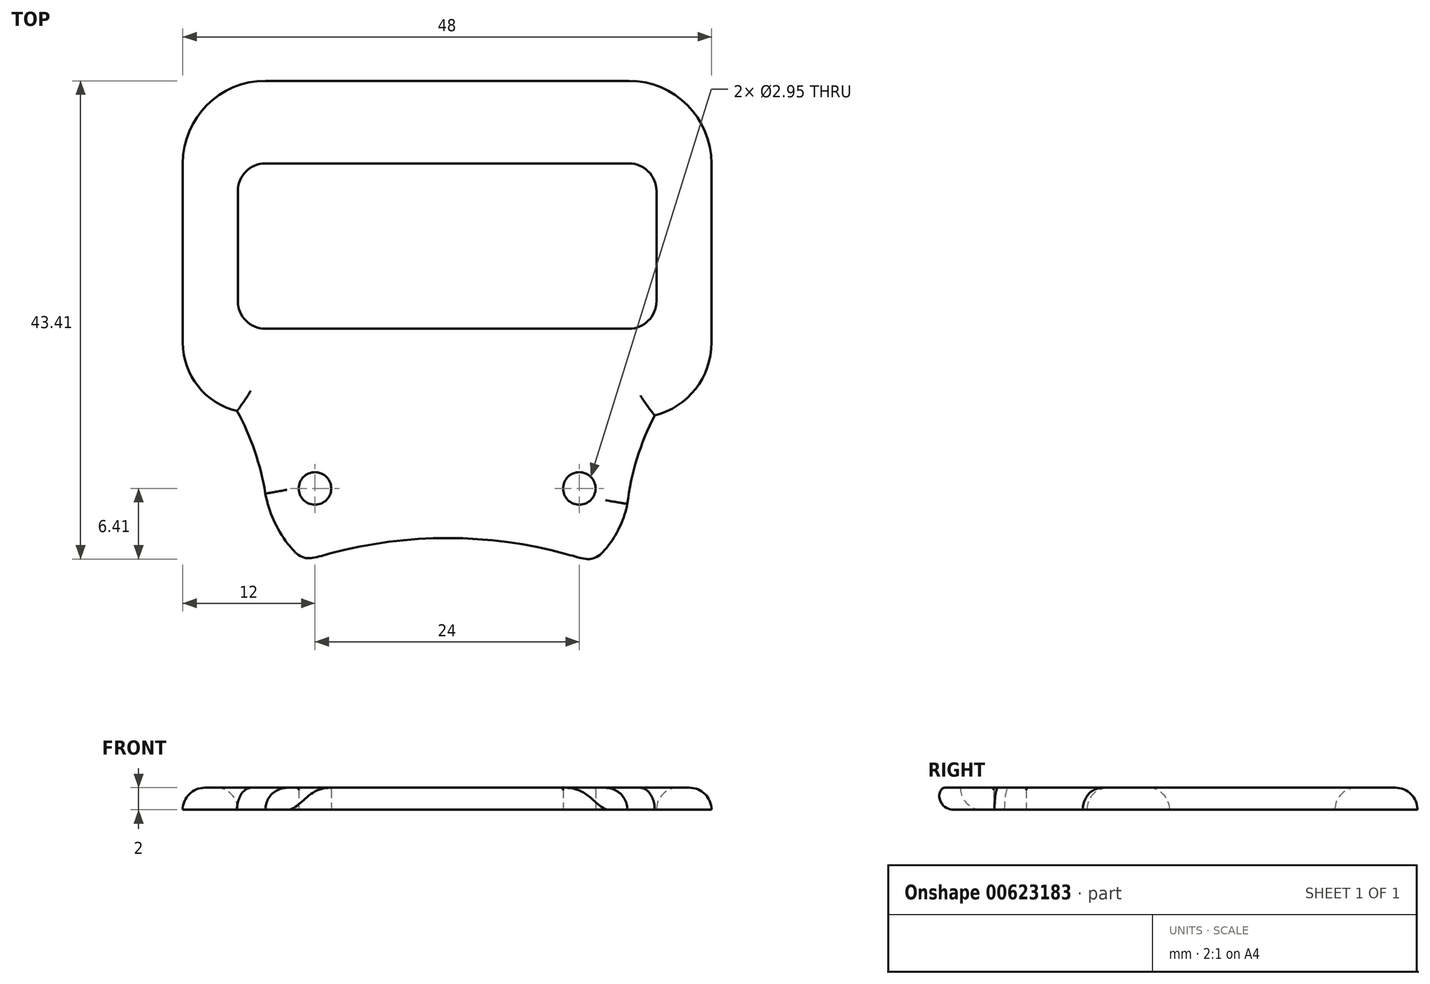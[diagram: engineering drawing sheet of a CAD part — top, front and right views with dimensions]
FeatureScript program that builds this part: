
annotation { "Feature Type Name" : "Feature", "Feature Type Description" : "" }
export const myFeature = defineFeature(function(context is Context, id is Id, definition is map)
    precondition{}
    {
        {
            var Q0;
            Q0=qCreatedBy(makeId("Top.planeOp"),FACE);
            var sketch = newSketch(context, id + "F0", { "sketchPlane" : qUnion([Q0])});
            skLineSegment(sketch, "E0.bottom", {"start": v(16.5, 2.5) * mm, "end": v(-16.5, 2.5) * mm});
            skLineSegment(sketch, "E0.left", {"start": v(19, 0) * mm, "end": v(19, 0) * mm});
            skLineSegment(sketch, "E0.right", {"start": v(-19, 0) * mm, "end": v(-19, 0) * mm});
            skPoint(sketch, "E0.middle", {"position": v(0, 0) * mm});
            skPoint(sketch, "E1.visualSharp", {"position": v(-19, 2.5) * mm});
            skArc(sketch, "E1.filletArc", {"start": v(-16.5, 2.5) * mm, "mid": v(-18.27, 1.77) * mm, "end": v(-19, 0) * mm});
            skPoint(sketch, "E2.visualSharp", {"position": v(-19, -2.5) * mm});
            skPoint(sketch, "E3.visualSharp", {"position": v(19, -2.5) * mm});
            skPoint(sketch, "E4.visualSharp", {"position": v(19, 2.5) * mm});
            skArc(sketch, "E5", {"start": v(-12.96, 23.6) * mm, "mid": v(0.12, 21.5) * mm, "end": v(13.2, 23.68) * mm});
            skLineSegment(sketch, "E6", {"start": v(0, 21.5) * mm, "end": v(0, 0) * mm, "construction": true});
            skArc(sketch, "E7", {"start": v(16.36, 18.4) * mm, "mid": v(17.24, 14.28) * mm, "end": v(18.84, 10.38) * mm});
            skArc(sketch, "E8", {"start": v(-19.07, 9.97) * mm, "mid": v(-17.47, 13.6) * mm, "end": v(-16.5, 17.47) * mm});
            skArc(sketch, "E9", {"start": v(16.5, 17.47) * mm, "mid": v(15.46, 20.9) * mm, "end": v(13.2, 23.68) * mm});
            skArc(sketch, "E10", {"start": v(-12.96, 23.6) * mm, "mid": v(-15.25, 20.83) * mm, "end": v(-16.5, 17.47) * mm});
            skArc(sketch, "E11", {"start": v(24, 3.75) * mm, "mid": v(22.56, 7.95) * mm, "end": v(18.84, 10.38) * mm});
            skArc(sketch, "E12", {"start": v(-19.07, 9.97) * mm, "mid": v(-22.62, 7.72) * mm, "end": v(-24, 3.75) * mm});
            skLineSegment(sketch, "E13.top", {"start": v(16.5, -12.5) * mm, "end": v(-16.5, -12.5) * mm});
            skLineSegment(sketch, "E13.left", {"start": v(12.81, -26.54) * mm, "end": v(12.81, -26.54) * mm});
            skLineSegment(sketch, "E13.right", {"start": v(-25.19, -26.54) * mm, "end": v(-25.19, -26.54) * mm});
            skPoint(sketch, "E13.middle", {"position": v(0, -10) * mm});
            skPoint(sketch, "E14.visualSharp", {"position": v(-19, -7.5) * mm});
            skPoint(sketch, "E15.visualSharp", {"position": v(-19, -12.5) * mm});
            skArc(sketch, "E15.filletArc", {"start": v(-19, -10) * mm, "mid": v(-18.27, -11.77) * mm, "end": v(-16.5, -12.5) * mm});
            skPoint(sketch, "E16.visualSharp", {"position": v(19, -12.5) * mm});
            skArc(sketch, "E16.filletArc", {"start": v(16.5, -12.5) * mm, "mid": v(18.27, -11.77) * mm, "end": v(19, -10) * mm});
            skPoint(sketch, "E17.visualSharp", {"position": v(19, -7.5) * mm});
            skLineSegment(sketch, "E18.bottom", {"start": v(16.5, -20) * mm, "end": v(-16.5, -20) * mm});
            skPoint(sketch, "E19.visualSharp", {"position": v(-24, -20) * mm});
            skArc(sketch, "E19.filletArc", {"start": v(-24, -12.5) * mm, "mid": v(-21.8, -17.8) * mm, "end": v(-16.5, -20) * mm});
            skPoint(sketch, "E20.visualSharp", {"position": v(24, -20) * mm});
            skArc(sketch, "E20.filletArc", {"start": v(16.5, -20) * mm, "mid": v(21.8, -17.8) * mm, "end": v(24, -12.5) * mm});
            skPoint(sketch, "E21.visualSharp", {"position": v(-24, 15) * mm});
            skPoint(sketch, "E22.visualSharp", {"position": v(24, 15) * mm});
            skLineSegment(sketch, "E23", {"start": v(0, -10) * mm, "end": v(0, 0) * mm, "construction": true});
            skPoint(sketch, "E23.endSnap0", {"position": v(0, -7.5) * mm});
            skLineSegment(sketch, "E24.left", {"start": v(12.81, -16.54) * mm, "end": v(12.81, -16.54) * mm});
            skLineSegment(sketch, "E24.right", {"start": v(-25.19, -16.54) * mm, "end": v(-25.19, -16.54) * mm});
            skArc(sketch, "E25.filletArc", {"start": v(19, 0) * mm, "mid": v(18.27, 1.77) * mm, "end": v(16.5, 2.5) * mm});
            skLineSegment(sketch, "E26", {"start": v(0, 13.56) * mm, "end": v(0, 30.56) * mm, "construction": true});
            skPoint(sketch, "E26.endSnap0", {"position": v(0, 13.56) * mm});
            skLineSegment(sketch, "E27", {"start": v(-24, 3.75) * mm, "end": v(-24, -12.5) * mm});
            skLineSegment(sketch, "E28", {"start": v(24, 3.75) * mm, "end": v(24, -12.5) * mm});
            skLineSegment(sketch, "E29", {"start": v(19, 0) * mm, "end": v(19, -10) * mm});
            skLineSegment(sketch, "E30", {"start": v(-19, 0) * mm, "end": v(-19, -10) * mm});
            skSolve(sketch);
        }
        {
            var Q0;
            Q0=qSketchRegion(id+"F0",true);
            extrude(context, id + "F1", {"entities" : qUnion([Q0]), "depth" : 2 * mm, "offsetDistance" : 25 * mm});
        }
        {
            var Q0;
            Q0=makeQuery(id+"F1.opExtrude","CAP_FACE",FACE,{"disambiguationData":[OSD([sQuery(id+"F0.wireOp",EDGE,"E0.bottom"),sQuery(id+"F0.wireOp",EDGE,"E0.top"),sQuery(id+"F0.wireOp",EDGE,"E1.filletArc"),sQuery(id+"F0.wireOp",EDGE,"E2.filletArc"),sQuery(id+"F0.wireOp",EDGE,"E3.filletArc"),sQuery(id+"F0.wireOp",EDGE,"E4.filletArc"),sQuery(id+"F0.wireOp",EDGE,"fSyda1dp-bRXo-veQ2-1vli-FGcmPaPxGLA8.bottom"),sQuery(id+"F0.wireOp",EDGE,"fSyda1dp-bRXo-veQ2-1vli-FGcmPaPxGLA8.left"),sQuery(id+"F0.wireOp",EDGE,"fSyda1dp-bRXo-veQ2-1vli-FGcmPaPxGLA8.right"),sQuery(id+"F0.wireOp",EDGE,"8e5c77ff-7d3e-47b9-92b3-3da03b7f7197.filletArc"),sQuery(id+"F0.wireOp",EDGE,"5fc17df5-e352-4315-a85b-becddfe47ee1.filletArc"),sQuery(id+"F0.wireOp",EDGE,"E5"),sQuery(id+"F0.wireOp",EDGE,"E7"),sQuery(id+"F0.wireOp",EDGE,"E8"),sQuery(id+"F0.wireOp",EDGE,"E9"),sQuery(id+"F0.wireOp",EDGE,"E10"),sQuery(id+"F0.wireOp",EDGE,"E11"),sQuery(id+"F0.wireOp",EDGE,"E12")])],"isStart":false});
            var sketch = newSketch(context, id + "F2", { "sketchPlane" : qUnion([Q0])});
            skLineSegment(sketch, "E31", {"start": v(0, 0) * mm, "end": v(0, 17) * mm, "construction": true});
            skLineSegment(sketch, "E32", {"start": v(0, 17) * mm, "end": v(-12, 17) * mm, "construction": true});
            skLineSegment(sketch, "E33", {"start": v(0, 17) * mm, "end": v(12, 17) * mm, "construction": true});
            skCircle(sketch, "E34", {"center": v(-12, 17) * mm, "radius": 1.48 * mm});
            skCircle(sketch, "E35", {"center": v(12, 17) * mm, "radius": 1.48 * mm});
            skSolve(sketch);
        }
        {
            var Q0;
            Q0=qSketchRegion(id+"F2",true);
            extrude(context, id + "F3", {"entities" : qUnion([Q0]), "operationType" : NewBodyOperationType.REMOVE, "oppositeDirection" : true, "depth" : 5 * mm, "offsetDistance" : 25 * mm});
        }
        {
            var Q0;
            Q0=makeQuery(id+"F1.opExtrude","CAP_EDGE",EDGE,{"disambiguationData":[OSD([sQuery(id+"F0.wireOp",EDGE,"fSyda1dp-bRXo-veQ2-1vli-FGcmPaPxGLA8.left")])],"isStart":true});
            var Q1;
            Q1=makeQuery(id+"F1.opExtrude","CAP_EDGE",EDGE,{"disambiguationData":[OSD([sQuery(id+"F0.wireOp",EDGE,"5fc17df5-e352-4315-a85b-becddfe47ee1.filletArc")])],"isStart":true});
            var Q2;
            Q2=makeQuery(id+"F1.opExtrude","CAP_EDGE",EDGE,{"disambiguationData":[OSD([sQuery(id+"F0.wireOp",EDGE,"fSyda1dp-bRXo-veQ2-1vli-FGcmPaPxGLA8.bottom")])],"isStart":true});
            var Q3;
            Q3=makeQuery(id+"F1.opExtrude","CAP_EDGE",EDGE,{"disambiguationData":[OSD([sQuery(id+"F0.wireOp",EDGE,"8e5c77ff-7d3e-47b9-92b3-3da03b7f7197.filletArc")])],"isStart":true});
            var Q4;
            Q4=makeQuery(id+"F1.opExtrude","CAP_EDGE",EDGE,{"disambiguationData":[OSD([sQuery(id+"F0.wireOp",EDGE,"fSyda1dp-bRXo-veQ2-1vli-FGcmPaPxGLA8.right")])],"isStart":true});
            var Q5;
            Q5=makeQuery(id+"F1.opExtrude","CAP_EDGE",EDGE,{"disambiguationData":[OSD([sQuery(id+"F0.wireOp",EDGE,"E12")])],"isStart":true});
            var Q6;
            Q6=makeQuery(id+"F1.opExtrude","CAP_EDGE",EDGE,{"disambiguationData":[OSD([sQuery(id+"F0.wireOp",EDGE,"E8")])],"isStart":true});
            var Q7;
            Q7=makeQuery(id+"F1.opExtrude","CAP_EDGE",EDGE,{"disambiguationData":[OSD([sQuery(id+"F0.wireOp",EDGE,"E10")])],"isStart":true});
            var Q8;
            Q8=makeQuery(id+"F1.opExtrude","CAP_EDGE",EDGE,{"disambiguationData":[OSD([sQuery(id+"F0.wireOp",EDGE,"E9")])],"isStart":true});
            var Q9;
            Q9=makeQuery(id+"F1.opExtrude","CAP_EDGE",EDGE,{"disambiguationData":[OSD([sQuery(id+"F0.wireOp",EDGE,"E7")])],"isStart":true});
            var Q10;
            Q10=makeQuery(id+"F1.opExtrude","CAP_EDGE",EDGE,{"disambiguationData":[OSD([sQuery(id+"F0.wireOp",EDGE,"E11")])],"isStart":true});
            var Q11;
            Q11=makeQuery(id+"F1.opExtrude","CAP_EDGE",EDGE,{"disambiguationData":[OSD([sQuery(id+"F0.wireOp",EDGE,"E0.bottom")])],"isStart":true});
            var Q12;
            Q12=makeQuery(id+"F1.opExtrude","CAP_EDGE",EDGE,{"disambiguationData":[OSD([sQuery(id+"F0.wireOp",EDGE,"E13.bottom")])],"isStart":true});
            fillet(context, id + "F4", {"entities" : qUnion([Q0, Q1, Q2, Q3, Q4, Q5, Q6, Q7, Q8, Q9, Q10, Q11, Q12]), "radius" : 2 * mm, "tangentPropagation" : true, "allowEdgeOverflow" : false});
        }
        {
            var Q0;
            Q0=makeQuery(id+"F1.opExtrude","CAP_EDGE",EDGE,{"disambiguationData":[OSD([sQuery(id+"F0.wireOp",EDGE,"E5")])],"isStart":false});
            fillet(context, id + "F5", {"entities" : qUnion([Q0]), "radius" : 2 * mm, "tangentPropagation" : true, "allowEdgeOverflow" : false});
        }
        {
            var Q0;
            Q0=makeQuery(id+"F3.boolean.opBoolean","COPY",EDGE,{"derivedFrom":makeQuery(id+"F3.opExtrude","CAP_EDGE",EDGE,{"disambiguationData":[OSD([sQuery(id+"F2.wireOp",EDGE,"E34")])],"isStart":true})});
            var Q1;
            Q1=makeQuery(id+"F3.boolean.opBoolean","COPY",EDGE,{"derivedFrom":makeQuery(id+"F3.opExtrude","CAP_EDGE",EDGE,{"disambiguationData":[OSD([sQuery(id+"F2.wireOp",EDGE,"E35")])],"isStart":true})});
            var Q2;
            Q2=makeQuery(id+"F3.boolean.opBoolean","INTERSECT",EDGE,{"derivedFrom":[makeQuery(id+"F1.opExtrude","CAP_FACE",FACE,{"disambiguationData":[OSD([sQuery(id+"F0.wireOp",EDGE,"E0.bottom"),sQuery(id+"F0.wireOp",EDGE,"E0.top"),sQuery(id+"F0.wireOp",EDGE,"E1.filletArc"),sQuery(id+"F0.wireOp",EDGE,"E2.filletArc"),sQuery(id+"F0.wireOp",EDGE,"E3.filletArc"),sQuery(id+"F0.wireOp",EDGE,"E4.filletArc"),sQuery(id+"F0.wireOp",EDGE,"fSyda1dp-bRXo-veQ2-1vli-FGcmPaPxGLA8.bottom"),sQuery(id+"F0.wireOp",EDGE,"fSyda1dp-bRXo-veQ2-1vli-FGcmPaPxGLA8.left"),sQuery(id+"F0.wireOp",EDGE,"fSyda1dp-bRXo-veQ2-1vli-FGcmPaPxGLA8.right"),sQuery(id+"F0.wireOp",EDGE,"8e5c77ff-7d3e-47b9-92b3-3da03b7f7197.filletArc"),sQuery(id+"F0.wireOp",EDGE,"5fc17df5-e352-4315-a85b-becddfe47ee1.filletArc"),sQuery(id+"F0.wireOp",EDGE,"E5"),sQuery(id+"F0.wireOp",EDGE,"E7"),sQuery(id+"F0.wireOp",EDGE,"E8"),sQuery(id+"F0.wireOp",EDGE,"E9"),sQuery(id+"F0.wireOp",EDGE,"E10"),sQuery(id+"F0.wireOp",EDGE,"E11"),sQuery(id+"F0.wireOp",EDGE,"E12")])],"isStart":true}),makeQuery(id+"F3.opExtrude","SWEPT_FACE",FACE,{"disambiguationData":[OSD([sQuery(id+"F2.wireOp",EDGE,"E34")])]})]});
            var Q3;
            Q3=makeQuery(id+"F3.boolean.opBoolean","INTERSECT",EDGE,{"derivedFrom":[makeQuery(id+"F1.opExtrude","CAP_FACE",FACE,{"disambiguationData":[OSD([sQuery(id+"F0.wireOp",EDGE,"E0.bottom"),sQuery(id+"F0.wireOp",EDGE,"E0.top"),sQuery(id+"F0.wireOp",EDGE,"E1.filletArc"),sQuery(id+"F0.wireOp",EDGE,"E2.filletArc"),sQuery(id+"F0.wireOp",EDGE,"E3.filletArc"),sQuery(id+"F0.wireOp",EDGE,"E4.filletArc"),sQuery(id+"F0.wireOp",EDGE,"fSyda1dp-bRXo-veQ2-1vli-FGcmPaPxGLA8.bottom"),sQuery(id+"F0.wireOp",EDGE,"fSyda1dp-bRXo-veQ2-1vli-FGcmPaPxGLA8.left"),sQuery(id+"F0.wireOp",EDGE,"fSyda1dp-bRXo-veQ2-1vli-FGcmPaPxGLA8.right"),sQuery(id+"F0.wireOp",EDGE,"8e5c77ff-7d3e-47b9-92b3-3da03b7f7197.filletArc"),sQuery(id+"F0.wireOp",EDGE,"5fc17df5-e352-4315-a85b-becddfe47ee1.filletArc"),sQuery(id+"F0.wireOp",EDGE,"E5"),sQuery(id+"F0.wireOp",EDGE,"E7"),sQuery(id+"F0.wireOp",EDGE,"E8"),sQuery(id+"F0.wireOp",EDGE,"E9"),sQuery(id+"F0.wireOp",EDGE,"E10"),sQuery(id+"F0.wireOp",EDGE,"E11"),sQuery(id+"F0.wireOp",EDGE,"E12")])],"isStart":true}),makeQuery(id+"F3.opExtrude","SWEPT_FACE",FACE,{"disambiguationData":[OSD([sQuery(id+"F2.wireOp",EDGE,"E35")])]})]});
            fillet(context, id + "F6", {"entities" : qUnion([Q0, Q1, Q2, Q3]), "radius" : .2 * mm, "tangentPropagation" : true, "allowEdgeOverflow" : false});
        }
        {
            var Q0;
            Q0=makeQuery(id+"F1.opExtrude","SWEPT_BODY",BODY,{"disambiguationData":[OSD([sQuery(id+"F0.wireOp",EDGE,"E0.bottom"),sQuery(id+"F0.wireOp",EDGE,"E0.top"),sQuery(id+"F0.wireOp",EDGE,"E1.filletArc"),sQuery(id+"F0.wireOp",EDGE,"E2.filletArc"),sQuery(id+"F0.wireOp",EDGE,"E3.filletArc"),sQuery(id+"F0.wireOp",EDGE,"E4.filletArc"),sQuery(id+"F0.wireOp",EDGE,"fSyda1dp-bRXo-veQ2-1vli-FGcmPaPxGLA8.bottom"),sQuery(id+"F0.wireOp",EDGE,"fSyda1dp-bRXo-veQ2-1vli-FGcmPaPxGLA8.left"),sQuery(id+"F0.wireOp",EDGE,"fSyda1dp-bRXo-veQ2-1vli-FGcmPaPxGLA8.right"),sQuery(id+"F0.wireOp",EDGE,"8e5c77ff-7d3e-47b9-92b3-3da03b7f7197.filletArc"),sQuery(id+"F0.wireOp",EDGE,"5fc17df5-e352-4315-a85b-becddfe47ee1.filletArc"),sQuery(id+"F0.wireOp",EDGE,"E5"),sQuery(id+"F0.wireOp",EDGE,"E7"),sQuery(id+"F0.wireOp",EDGE,"E8"),sQuery(id+"F0.wireOp",EDGE,"E9"),sQuery(id+"F0.wireOp",EDGE,"E10"),sQuery(id+"F0.wireOp",EDGE,"E11"),sQuery(id+"F0.wireOp",EDGE,"E12")])]});
            var Q1;
            {var subQ0=sQuery(id+"F0.wireOp",EDGE,"E0.bottom");Q1=makeQuery(id+"F4.opFillet","BLEND_EDGE",EDGE,{"blendedFrom":[makeQuery(id+"F1.opExtrude","CAP_EDGE",EDGE,{"disambiguationData":[OSD([subQ0])],"isStart":true}),makeQuery(id+"F1.opExtrude","CAP_FACE",FACE,{"disambiguationData":[OSD([subQ0,sQuery(id+"F0.wireOp",EDGE,"E0.top"),sQuery(id+"F0.wireOp",EDGE,"E1.filletArc"),sQuery(id+"F0.wireOp",EDGE,"E2.filletArc"),sQuery(id+"F0.wireOp",EDGE,"E3.filletArc"),sQuery(id+"F0.wireOp",EDGE,"E4.filletArc"),sQuery(id+"F0.wireOp",EDGE,"fSyda1dp-bRXo-veQ2-1vli-FGcmPaPxGLA8.bottom"),sQuery(id+"F0.wireOp",EDGE,"fSyda1dp-bRXo-veQ2-1vli-FGcmPaPxGLA8.left"),sQuery(id+"F0.wireOp",EDGE,"fSyda1dp-bRXo-veQ2-1vli-FGcmPaPxGLA8.right"),sQuery(id+"F0.wireOp",EDGE,"8e5c77ff-7d3e-47b9-92b3-3da03b7f7197.filletArc"),sQuery(id+"F0.wireOp",EDGE,"5fc17df5-e352-4315-a85b-becddfe47ee1.filletArc"),sQuery(id+"F0.wireOp",EDGE,"E5"),sQuery(id+"F0.wireOp",EDGE,"E7"),sQuery(id+"F0.wireOp",EDGE,"E8"),sQuery(id+"F0.wireOp",EDGE,"E9"),sQuery(id+"F0.wireOp",EDGE,"E10"),sQuery(id+"F0.wireOp",EDGE,"E11"),sQuery(id+"F0.wireOp",EDGE,"E12")])],"isStart":false})],"blendedInto":[makeQuery(id+"F1.opExtrude","CAP_FACE",FACE,{"disambiguationData":[OSD([subQ0,sQuery(id+"F0.wireOp",EDGE,"E0.top"),sQuery(id+"F0.wireOp",EDGE,"E1.filletArc"),sQuery(id+"F0.wireOp",EDGE,"E2.filletArc"),sQuery(id+"F0.wireOp",EDGE,"E3.filletArc"),sQuery(id+"F0.wireOp",EDGE,"E4.filletArc"),sQuery(id+"F0.wireOp",EDGE,"fSyda1dp-bRXo-veQ2-1vli-FGcmPaPxGLA8.bottom"),sQuery(id+"F0.wireOp",EDGE,"fSyda1dp-bRXo-veQ2-1vli-FGcmPaPxGLA8.left"),sQuery(id+"F0.wireOp",EDGE,"fSyda1dp-bRXo-veQ2-1vli-FGcmPaPxGLA8.right"),sQuery(id+"F0.wireOp",EDGE,"8e5c77ff-7d3e-47b9-92b3-3da03b7f7197.filletArc"),sQuery(id+"F0.wireOp",EDGE,"5fc17df5-e352-4315-a85b-becddfe47ee1.filletArc"),sQuery(id+"F0.wireOp",EDGE,"E5"),sQuery(id+"F0.wireOp",EDGE,"E7"),sQuery(id+"F0.wireOp",EDGE,"E8"),sQuery(id+"F0.wireOp",EDGE,"E9"),sQuery(id+"F0.wireOp",EDGE,"E10"),sQuery(id+"F0.wireOp",EDGE,"E11"),sQuery(id+"F0.wireOp",EDGE,"E12")])],"isStart":false})]});}
            transform(context, id + "F7", {"entities" : qUnion([Q0]), "transformType" : TransformType.ROTATION, "transformAxis" : qUnion([Q1]), "angle" : 180 * degree, "makeCopy" : false});
        }
    });
